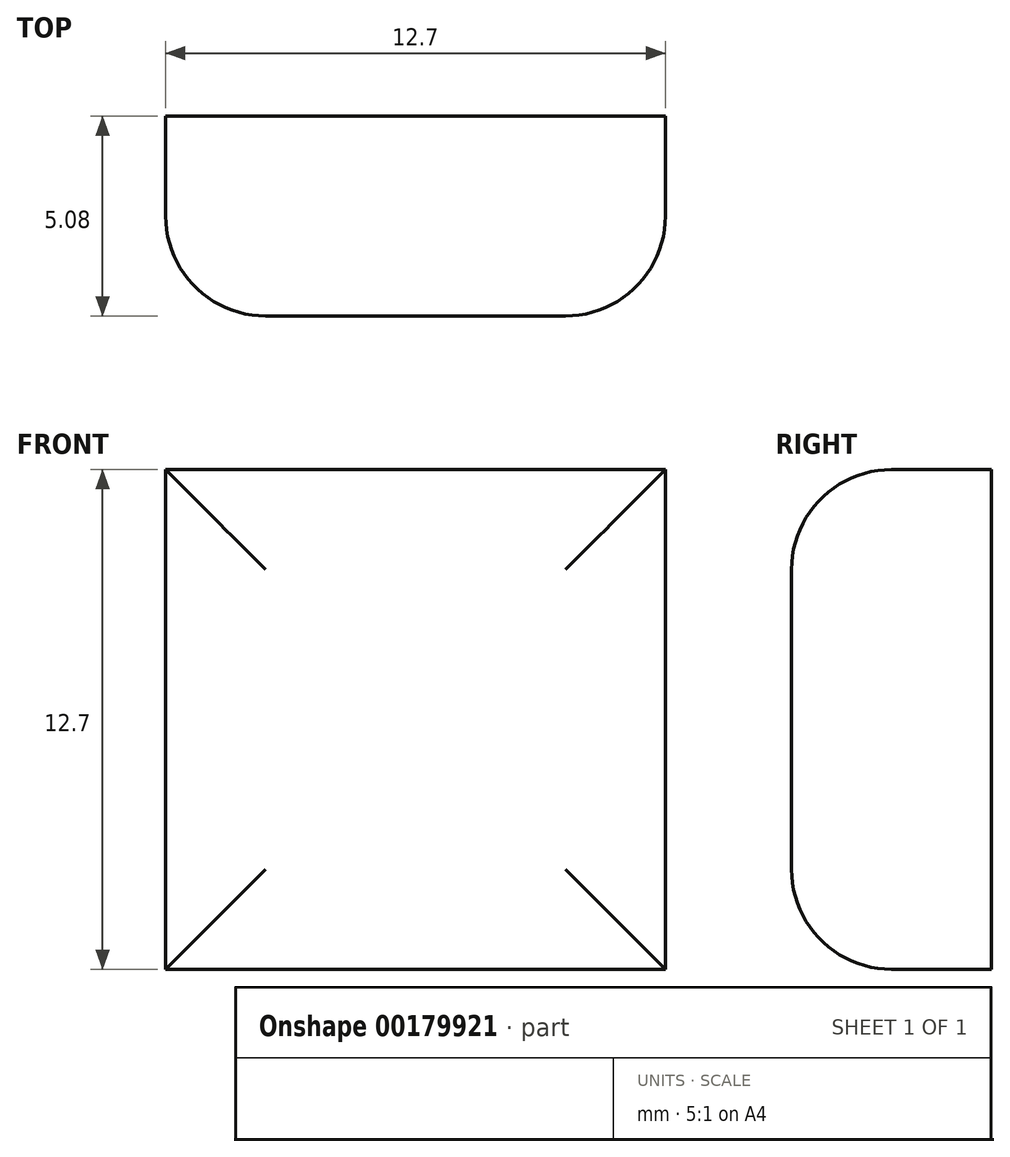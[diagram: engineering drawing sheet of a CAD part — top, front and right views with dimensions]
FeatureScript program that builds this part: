
annotation { "Feature Type Name" : "Feature", "Feature Type Description" : "" }
export const myFeature = defineFeature(function(context is Context, id is Id, definition is map)
    precondition{}
    {
        {
            var Q0;
            Q0=qCreatedBy(makeId("Front.planeOp"),FACE);
            var sketch = newSketch(context, id + "F0", { "sketchPlane" : qUnion([Q0])});
            skLineSegment(sketch, "E0.bottom", {"start": v(0, 0) * mm, "end": v(-12.7, 0) * mm});
            skLineSegment(sketch, "E0.top", {"start": v(0, 12.7) * mm, "end": v(-12.7, 12.7) * mm});
            skLineSegment(sketch, "E0.left", {"start": v(0, 0) * mm, "end": v(0, 12.7) * mm});
            skLineSegment(sketch, "E0.right", {"start": v(-12.7, 0) * mm, "end": v(-12.7, 12.7) * mm});
            skSolve(sketch);
        }
        {
            var Q0;
            Q0=makeQuery(id+"F0.imprint","IMPRINT",FACE,{"disambiguationData":[TD([[makeQuery(id+"F0.imprint","IMPRINT",EDGE,{"derivedFrom":sQuery(id+"F0.wireOp",EDGE,"E0.bottom")}),-1.0]])]});
            extrude(context, id + "F1", {"entities" : qUnion([Q0]), "depth" : 5.08 * mm});
        }
        {
            var Q0;
            Q0=makeQuery(id+"F1.opExtrude","CAP_EDGE",EDGE,{"disambiguationData":[OSD([sQuery(id+"F0.wireOp",EDGE,"E0.top")])],"isStart":false});
            var Q1;
            Q1=makeQuery(id+"F1.opExtrude","CAP_EDGE",EDGE,{"disambiguationData":[OSD([sQuery(id+"F0.wireOp",EDGE,"E0.left")])],"isStart":false});
            var Q2;
            Q2=makeQuery(id+"F1.opExtrude","CAP_EDGE",EDGE,{"disambiguationData":[OSD([sQuery(id+"F0.wireOp",EDGE,"E0.right")])],"isStart":false});
            var Q3;
            Q3=makeQuery(id+"F1.opExtrude","CAP_EDGE",EDGE,{"disambiguationData":[OSD([sQuery(id+"F0.wireOp",EDGE,"E0.bottom")])],"isStart":false});
            fillet(context, id + "F2", {"entities" : qUnion([Q0, Q1, Q2, Q3]), "radius" : 2.54 * mm, "tangentPropagation" : true, "allowEdgeOverflow" : false});
        }
    });
